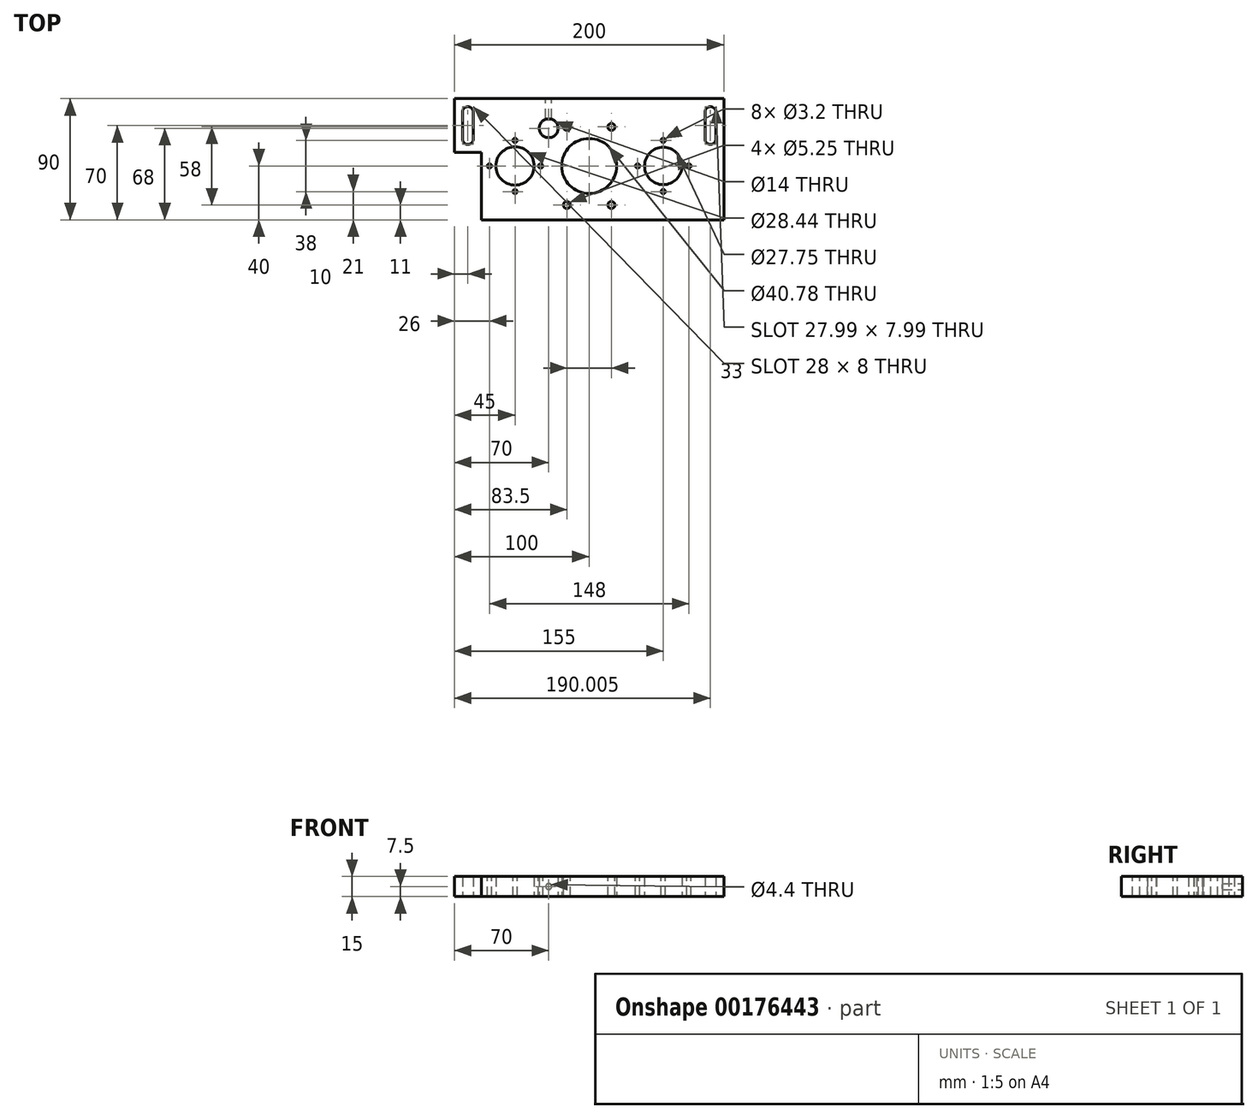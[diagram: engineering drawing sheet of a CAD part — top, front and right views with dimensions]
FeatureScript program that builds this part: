
annotation { "Feature Type Name" : "Feature", "Feature Type Description" : "" }
export const myFeature = defineFeature(function(context is Context, id is Id, definition is map)
    precondition{}
    {
        {
            var Q0;
            Q0=qCreatedBy(makeId("Top.planeOp"),FACE);
            var sketch = newSketch(context, id + "F0", { "sketchPlane" : qUnion([Q0])});
            skLineSegment(sketch, "E0.bottom", {"start": v(100, -45) * mm, "end": v(-80, -45) * mm});
            skLineSegment(sketch, "E0.top", {"start": v(100, 45) * mm, "end": v(-100, 45) * mm});
            skLineSegment(sketch, "E0.left", {"start": v(100, -45) * mm, "end": v(100, 45) * mm});
            skLineSegment(sketch, "E0.right", {"start": v(-100, 5) * mm, "end": v(-100, 45) * mm});
            skPoint(sketch, "E0.middle", {"position": v(0, 0) * mm});
            skLineSegment(sketch, "E1", {"start": v(-100, 5) * mm, "end": v(-80, 5) * mm});
            skLineSegment(sketch, "E2", {"start": v(-80, 5) * mm, "end": v(-80, -45) * mm});
            skPoint(sketch, "E3.orphan", {"position": v(-100, -45) * mm});
            skCircle(sketch, "E4", {"center": v(-55, -5) * mm, "radius": 14.22 * mm});
            skCircle(sketch, "E5", {"center": v(55, -5) * mm, "radius": 13.87 * mm});
            skCircle(sketch, "E6", {"center": v(0, -5) * mm, "radius": 20.4 * mm});
            skArc(sketch, "E7", {"start": v(-86, 34.95) * mm, "mid": v(-89.98, 39) * mm, "end": v(-94, 35) * mm});
            skArc(sketch, "E8", {"start": v(-94, 15.14) * mm, "mid": v(-90.05, 11) * mm, "end": v(-86, 15.05) * mm});
            skArc(sketch, "E9", {"start": v(94, 35) * mm, "mid": v(89.85, 39) * mm, "end": v(86.01, 34.7) * mm});
            skArc(sketch, "E10", {"start": v(86.01, 15.3) * mm, "mid": v(89.85, 11) * mm, "end": v(94, 15) * mm});
            skLineSegment(sketch, "E11", {"start": v(-94, 15.14) * mm, "end": v(-94, 35) * mm});
            skLineSegment(sketch, "E12", {"start": v(-86, 35.05) * mm, "end": v(-86, 14.95) * mm});
            skLineSegment(sketch, "E13", {"start": v(86.01, 35.3) * mm, "end": v(86.01, 14.7) * mm});
            skLineSegment(sketch, "E14", {"start": v(94, 35) * mm, "end": v(94, 15) * mm});
            skCircle(sketch, "E15", {"center": v(-30, 23) * mm, "radius": 7 * mm});
            skSolve(sketch);
        }
        {
            var Q0;
            Q0=makeQuery(id+"F0.imprint","IMPRINT",FACE,{"disambiguationData":[TD([[makeQuery(id+"F0.imprint","IMPRINT",EDGE,{"derivedFrom":sQuery(id+"F0.wireOp",EDGE,"E0.bottom")}),-1.0]])]});
            extrude(context, id + "F1", {"entities" : qUnion([Q0]), "depth" : 15 * mm});
        }
        {
            var Q0;
            Q0=makeQuery(id+"F1.opExtrude","CAP_FACE",FACE,{"disambiguationData":[OSD([sQuery(id+"F0.wireOp",EDGE,"E0.bottom"),sQuery(id+"F0.wireOp",EDGE,"E0.top"),sQuery(id+"F0.wireOp",EDGE,"E0.left"),sQuery(id+"F0.wireOp",EDGE,"E0.right"),sQuery(id+"F0.wireOp",EDGE,"E1"),sQuery(id+"F0.wireOp",EDGE,"E2"),sQuery(id+"F0.wireOp",EDGE,"E4"),sQuery(id+"F0.wireOp",EDGE,"E5"),sQuery(id+"F0.wireOp",EDGE,"E6"),sQuery(id+"F0.wireOp",EDGE,"E7"),sQuery(id+"F0.wireOp",EDGE,"E8"),sQuery(id+"F0.wireOp",EDGE,"E9"),sQuery(id+"F0.wireOp",EDGE,"E10"),sQuery(id+"F0.wireOp",EDGE,"E11"),sQuery(id+"F0.wireOp",EDGE,"E12"),sQuery(id+"F0.wireOp",EDGE,"E13"),sQuery(id+"F0.wireOp",EDGE,"E14"),sQuery(id+"F0.wireOp",EDGE,"E15")])],"isStart":false});
            var sketch = newSketch(context, id + "F2", { "sketchPlane" : qUnion([Q0])});
            skCircle(sketch, "E16", {"center": v(-55, 14) * mm, "radius": 1.6 * mm});
            skCircle(sketch, "E17", {"center": v(-36, -5) * mm, "radius": 1.64 * mm});
            skCircle(sketch, "E18", {"center": v(-55, -24) * mm, "radius": 1.78 * mm});
            skCircle(sketch, "E19", {"center": v(-74, -5) * mm, "radius": 1.88 * mm});
            skCircle(sketch, "E20", {"center": v(36, -5) * mm, "radius": 2.4 * mm});
            skCircle(sketch, "E21", {"center": v(55, 14) * mm, "radius": 2.05 * mm});
            skCircle(sketch, "E22", {"center": v(74, -5) * mm, "radius": 1.89 * mm});
            skCircle(sketch, "E23", {"center": v(55, -24) * mm, "radius": 1.99 * mm});
            skSolve(sketch);
        }
        {
            var Q0;
            Q0=sQuery(id+"F2.wireOp",VERTEX,"E19.center");
            var Q1;
            Q1=sQuery(id+"F2.wireOp",VERTEX,"E16.center");
            var Q2;
            Q2=sQuery(id+"F2.wireOp",VERTEX,"E17.center");
            var Q3;
            Q3=sQuery(id+"F2.wireOp",VERTEX,"E18.center");
            var Q4;
            Q4=sQuery(id+"F2.wireOp",VERTEX,"E20.center");
            var Q5;
            Q5=sQuery(id+"F2.wireOp",VERTEX,"E21.center");
            var Q6;
            Q6=sQuery(id+"F2.wireOp",VERTEX,"E22.center");
            var Q7;
            Q7=sQuery(id+"F2.wireOp",VERTEX,"E23.center");
            var Q8;
            Q8=makeQuery(id+"F1.opExtrude","SWEPT_BODY",BODY,{"disambiguationData":[OSD([sQuery(id+"F0.wireOp",EDGE,"E0.bottom"),sQuery(id+"F0.wireOp",EDGE,"E0.top"),sQuery(id+"F0.wireOp",EDGE,"E0.left"),sQuery(id+"F0.wireOp",EDGE,"E0.right"),sQuery(id+"F0.wireOp",EDGE,"E1"),sQuery(id+"F0.wireOp",EDGE,"E2"),sQuery(id+"F0.wireOp",EDGE,"E4"),sQuery(id+"F0.wireOp",EDGE,"E5"),sQuery(id+"F0.wireOp",EDGE,"E6"),sQuery(id+"F0.wireOp",EDGE,"E7"),sQuery(id+"F0.wireOp",EDGE,"E8"),sQuery(id+"F0.wireOp",EDGE,"E9"),sQuery(id+"F0.wireOp",EDGE,"E10"),sQuery(id+"F0.wireOp",EDGE,"E11"),sQuery(id+"F0.wireOp",EDGE,"E12"),sQuery(id+"F0.wireOp",EDGE,"E13"),sQuery(id+"F0.wireOp",EDGE,"E14"),sQuery(id+"F0.wireOp",EDGE,"E15")])]});
            hole(context, id + "F3", {"style" : HoleStyle.SIMPLE, "endStyle" : HoleEndStyle.THROUGH, "standardTappedOrClearance" : lookupTablePath({ "standard" : "ISO", "engagement" : "75%", "pitch" : "0.75 mm", "size" : "M4", "type" : "Tapped" }), "standardBlindInLast" : lookupTablePath({ "standard" : "ISO", "engagement" : "75%", "pitch" : "0.75 mm", "size" : "M4", "type" : "Tapped" }), "holeDiameter" : 3.2 * mm, "startFromSketch" : true, "locations" : qUnion([Q0, Q1, Q2, Q3, Q4, Q5, Q6, Q7]), "scope" : qUnion([Q8]), "isTappedThrough" : true, "showTappedDepth" : true});
        }
        {
            var Q0;
            Q0=makeQuery(id+"F1.opExtrude","CAP_FACE",FACE,{"disambiguationData":[OSD([sQuery(id+"F0.wireOp",EDGE,"E0.bottom"),sQuery(id+"F0.wireOp",EDGE,"E0.top"),sQuery(id+"F0.wireOp",EDGE,"E0.left"),sQuery(id+"F0.wireOp",EDGE,"E0.right"),sQuery(id+"F0.wireOp",EDGE,"E1"),sQuery(id+"F0.wireOp",EDGE,"E2"),sQuery(id+"F0.wireOp",EDGE,"E4"),sQuery(id+"F0.wireOp",EDGE,"E5"),sQuery(id+"F0.wireOp",EDGE,"E6"),sQuery(id+"F0.wireOp",EDGE,"E7"),sQuery(id+"F0.wireOp",EDGE,"E8"),sQuery(id+"F0.wireOp",EDGE,"E9"),sQuery(id+"F0.wireOp",EDGE,"E10"),sQuery(id+"F0.wireOp",EDGE,"E11"),sQuery(id+"F0.wireOp",EDGE,"E12"),sQuery(id+"F0.wireOp",EDGE,"E13"),sQuery(id+"F0.wireOp",EDGE,"E14"),sQuery(id+"F0.wireOp",EDGE,"E15")])],"isStart":false});
            var sketch = newSketch(context, id + "F4", { "sketchPlane" : qUnion([Q0])});
            skCircle(sketch, "E24", {"center": v(-16.5, 24) * mm, "radius": 2.56 * mm});
            skCircle(sketch, "E25", {"center": v(16.5, 24) * mm, "radius": 2.38 * mm});
            skCircle(sketch, "E26", {"center": v(16.5, -34) * mm, "radius": 2.89 * mm});
            skCircle(sketch, "E27", {"center": v(-16.5, -34) * mm, "radius": 3.1 * mm});
            skSolve(sketch);
        }
        {
            var Q0;
            Q0=sQuery(id+"F4.wireOp",VERTEX,"E24.center");
            var Q1;
            Q1=sQuery(id+"F4.wireOp",VERTEX,"E25.center");
            var Q2;
            Q2=sQuery(id+"F4.wireOp",VERTEX,"E26.center");
            var Q3;
            Q3=sQuery(id+"F4.wireOp",VERTEX,"E27.center");
            var Q4;
            Q4=makeQuery(id+"F1.opExtrude","SWEPT_BODY",BODY,{"disambiguationData":[OSD([sQuery(id+"F0.wireOp",EDGE,"E0.bottom"),sQuery(id+"F0.wireOp",EDGE,"E0.top"),sQuery(id+"F0.wireOp",EDGE,"E0.left"),sQuery(id+"F0.wireOp",EDGE,"E0.right"),sQuery(id+"F0.wireOp",EDGE,"E1"),sQuery(id+"F0.wireOp",EDGE,"E2"),sQuery(id+"F0.wireOp",EDGE,"E4"),sQuery(id+"F0.wireOp",EDGE,"E5"),sQuery(id+"F0.wireOp",EDGE,"E6"),sQuery(id+"F0.wireOp",EDGE,"E7"),sQuery(id+"F0.wireOp",EDGE,"E8"),sQuery(id+"F0.wireOp",EDGE,"E9"),sQuery(id+"F0.wireOp",EDGE,"E10"),sQuery(id+"F0.wireOp",EDGE,"E11"),sQuery(id+"F0.wireOp",EDGE,"E12"),sQuery(id+"F0.wireOp",EDGE,"E13"),sQuery(id+"F0.wireOp",EDGE,"E14"),sQuery(id+"F0.wireOp",EDGE,"E15")])]});
            hole(context, id + "F5", {"style" : HoleStyle.SIMPLE, "endStyle" : HoleEndStyle.THROUGH, "standardTappedOrClearance" : lookupTablePath({ "standard" : "ISO", "engagement" : "75%", "pitch" : "0.75 mm", "size" : "M6", "type" : "Tapped" }), "standardBlindInLast" : lookupTablePath({ "standard" : "ISO", "engagement" : "75%", "pitch" : "0.75 mm", "size" : "M6", "type" : "Tapped" }), "holeDiameter" : 5.25 * mm, "startFromSketch" : true, "locations" : qUnion([Q0, Q1, Q2, Q3]), "scope" : qUnion([Q4]), "isTappedThrough" : true, "majorDiameter" : 6 * mm, "showTappedDepth" : true});
        }
        {
            var Q0;
            Q0=makeQuery(id+"F1.opExtrude","SWEPT_FACE",FACE,{"disambiguationData":[OSD([sQuery(id+"F0.wireOp",EDGE,"E0.top")])]});
            var sketch = newSketch(context, id + "F6", { "sketchPlane" : qUnion([Q0])});
            skCircle(sketch, "E28", {"center": v(30, 7.5) * mm, "radius": 1.77 * mm});
            skSolve(sketch);
        }
        {
            var Q0;
            Q0=sQuery(id+"F6.wireOp",VERTEX,"E28.center");
            var Q1;
            Q1=makeQuery(id+"F1.opExtrude","SWEPT_BODY",BODY,{"disambiguationData":[OSD([sQuery(id+"F0.wireOp",EDGE,"E0.bottom"),sQuery(id+"F0.wireOp",EDGE,"E0.top"),sQuery(id+"F0.wireOp",EDGE,"E0.left"),sQuery(id+"F0.wireOp",EDGE,"E0.right"),sQuery(id+"F0.wireOp",EDGE,"E1"),sQuery(id+"F0.wireOp",EDGE,"E2"),sQuery(id+"F0.wireOp",EDGE,"E4"),sQuery(id+"F0.wireOp",EDGE,"E5"),sQuery(id+"F0.wireOp",EDGE,"E6"),sQuery(id+"F0.wireOp",EDGE,"E7"),sQuery(id+"F0.wireOp",EDGE,"E8"),sQuery(id+"F0.wireOp",EDGE,"E9"),sQuery(id+"F0.wireOp",EDGE,"E10"),sQuery(id+"F0.wireOp",EDGE,"E11"),sQuery(id+"F0.wireOp",EDGE,"E12"),sQuery(id+"F0.wireOp",EDGE,"E13"),sQuery(id+"F0.wireOp",EDGE,"E14"),sQuery(id+"F0.wireOp",EDGE,"E15")])]});
            hole(context, id + "F7", {"style" : HoleStyle.SIMPLE, "endStyle" : HoleEndStyle.BLIND, "standardTappedOrClearance" : lookupTablePath({ "standard" : "ISO", "fit" : "Normal", "size" : "M4", "type" : "Clearance" }), "standardBlindInLast" : lookupTablePath({ "fit" : "Standard", "standard" : "ISO", "size" : "M4", "type" : "Clearance" }), "holeDiameter" : 4.4 * mm, "holeDepth" : 15 * mm, "startFromSketch" : true, "locations" : qUnion([Q0]), "scope" : qUnion([Q1])});
        }
    });
